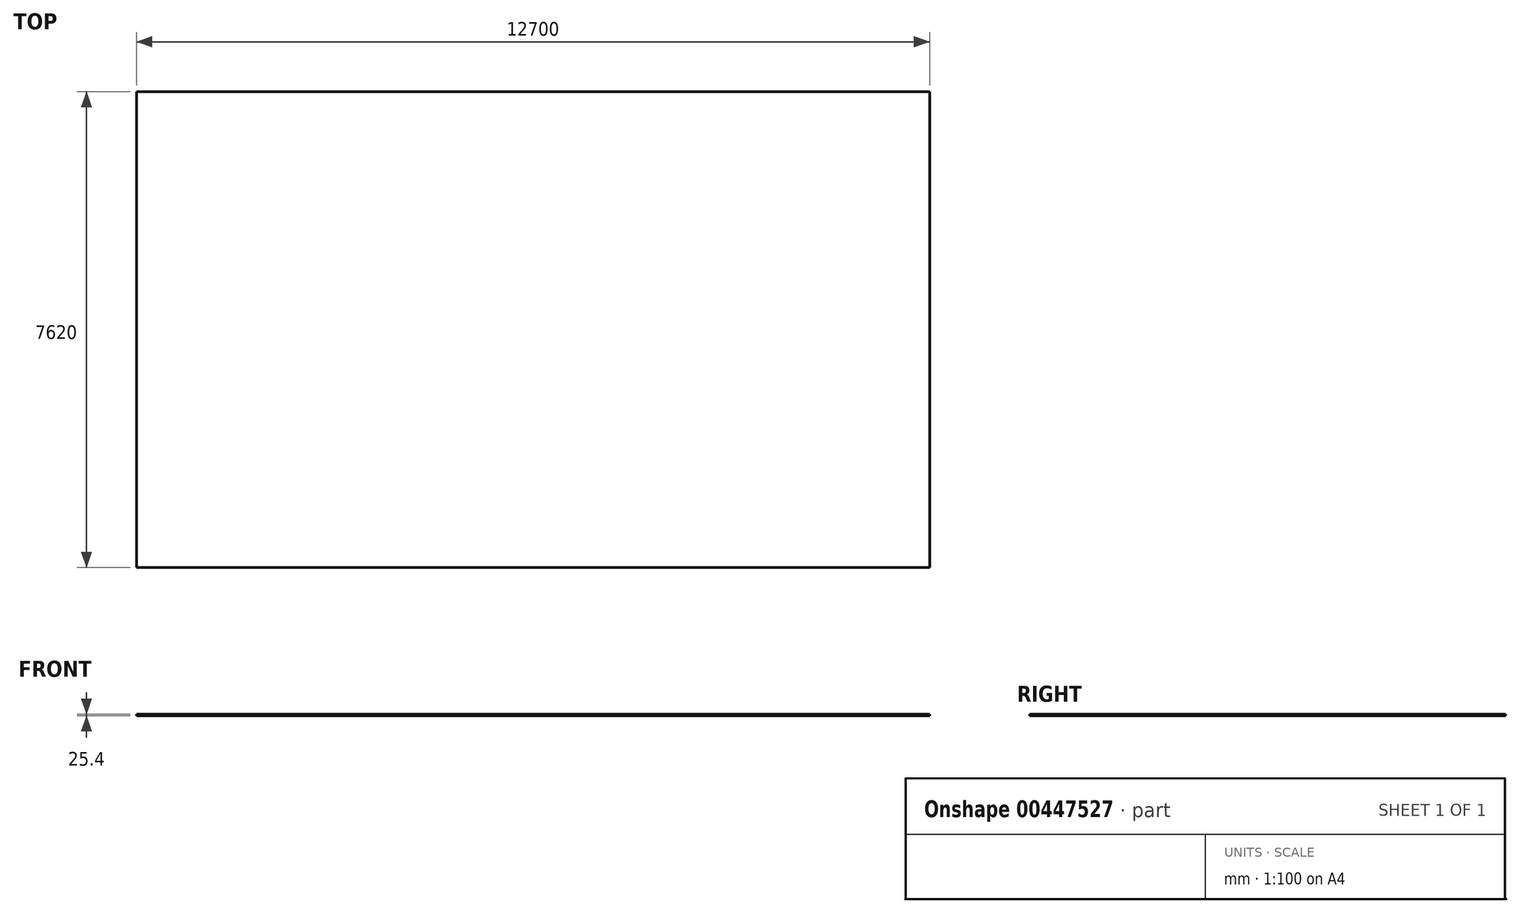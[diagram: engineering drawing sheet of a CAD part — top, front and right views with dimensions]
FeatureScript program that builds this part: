
annotation { "Feature Type Name" : "Feature", "Feature Type Description" : "" }
export const myFeature = defineFeature(function(context is Context, id is Id, definition is map)
    precondition{}
    {
        {
            var Q0;
            Q0=qCreatedBy(makeId("Top.planeOp"),FACE);
            var sketch = newSketch(context, id + "F0", { "sketchPlane" : qUnion([Q0])});
            skLineSegment(sketch, "E0.bottom", {"start": v(6350, -3810) * mm, "end": v(-6350, -3810) * mm});
            skLineSegment(sketch, "E0.top", {"start": v(6350, 3810) * mm, "end": v(-6350, 3810) * mm});
            skLineSegment(sketch, "E0.left", {"start": v(6350, -3810) * mm, "end": v(6350, 3810) * mm});
            skLineSegment(sketch, "E0.right", {"start": v(-6350, -3810) * mm, "end": v(-6350, 3810) * mm});
            skPoint(sketch, "E0.middle", {"position": v(0, 0) * mm});
            skSolve(sketch);
        }
        {
            var Q0;
            Q0 = qSketchRegion(id + "F0", true);
            extrude(context, id + "F1", {"entities" : qUnion([Q0]), "depth" : 25.4 * mm});
        }
    });
